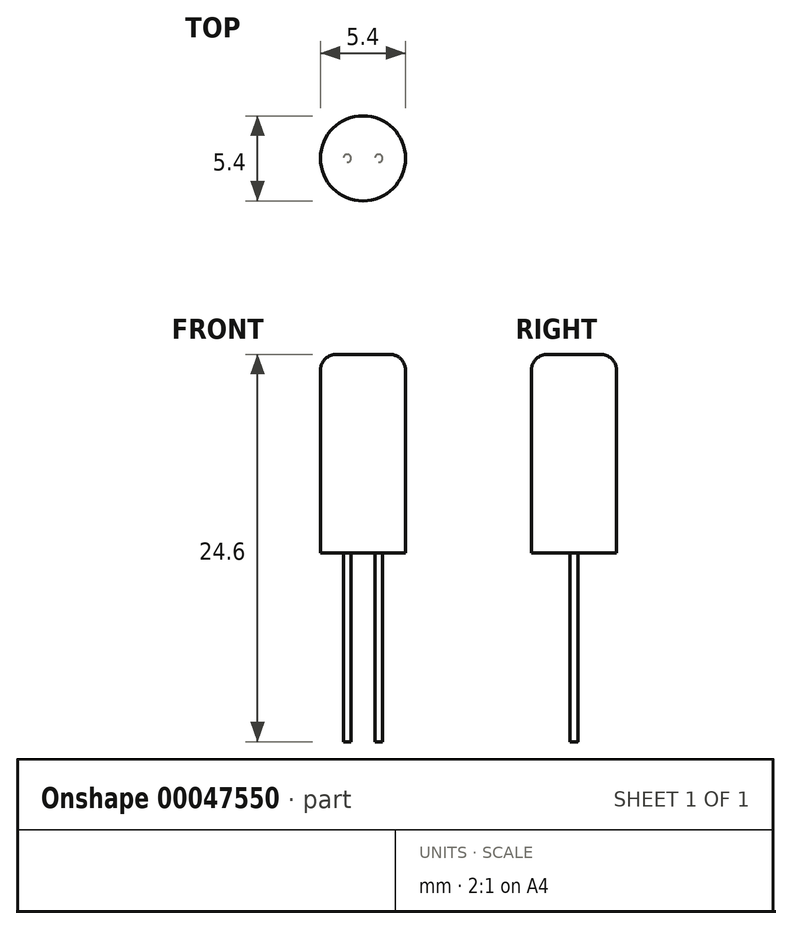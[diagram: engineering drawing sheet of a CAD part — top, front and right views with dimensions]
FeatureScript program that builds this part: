
annotation { "Feature Type Name" : "Feature", "Feature Type Description" : "" }
export const myFeature = defineFeature(function(context is Context, id is Id, definition is map)
    precondition{}
    {
        {
            var Q0;
            Q0=qCreatedBy(makeId("Top.planeOp"),FACE);
            var sketch = newSketch(context, id + "F0", { "sketchPlane" : qUnion([Q0])});
            skCircle(sketch, "E0", {"center": v(0, 0) * mm, "radius": 2.7 * mm});
            skSolve(sketch);
        }
        {
            var Q0;
            Q0 = qSketchRegion(id + "F0", true);
            extrude(context, id + "F1", {"entities" : qUnion([Q0]), "depth" : 12.6 * mm});
        }
        {
            var Q0;
            Q0=makeQuery(id+"F1.opExtrude","CAP_EDGE",EDGE,{"disambiguationData":[OSD([sQuery(id+"F0.wireOp",EDGE,"E0")])],"isStart":false});
            fillet(context, id + "F2", {"entities" : qUnion([Q0]), "radius" : 1 * mm, "tangentPropagation" : true, "allowEdgeOverflow" : false});
        }
        {
            var Q0;
            Q0=qCreatedBy(makeId("Top.planeOp"),FACE);
            var sketch = newSketch(context, id + "F3", { "sketchPlane" : qUnion([Q0])});
            skCircle(sketch, "E1", {"center": v(-1, 0) * mm, "radius": 0.25 * mm});
            skCircle(sketch, "E2", {"center": v(1, 0) * mm, "radius": 0.25 * mm});
            skSolve(sketch);
        }
        {
            var Q0;
            Q0 = qSketchRegion(id + "F3", true);
            extrude(context, id + "F4", {"entities" : qUnion([Q0]), "operationType" : NewBodyOperationType.ADD, "oppositeDirection" : true, "depth" : 12 * mm});
        }
    });
